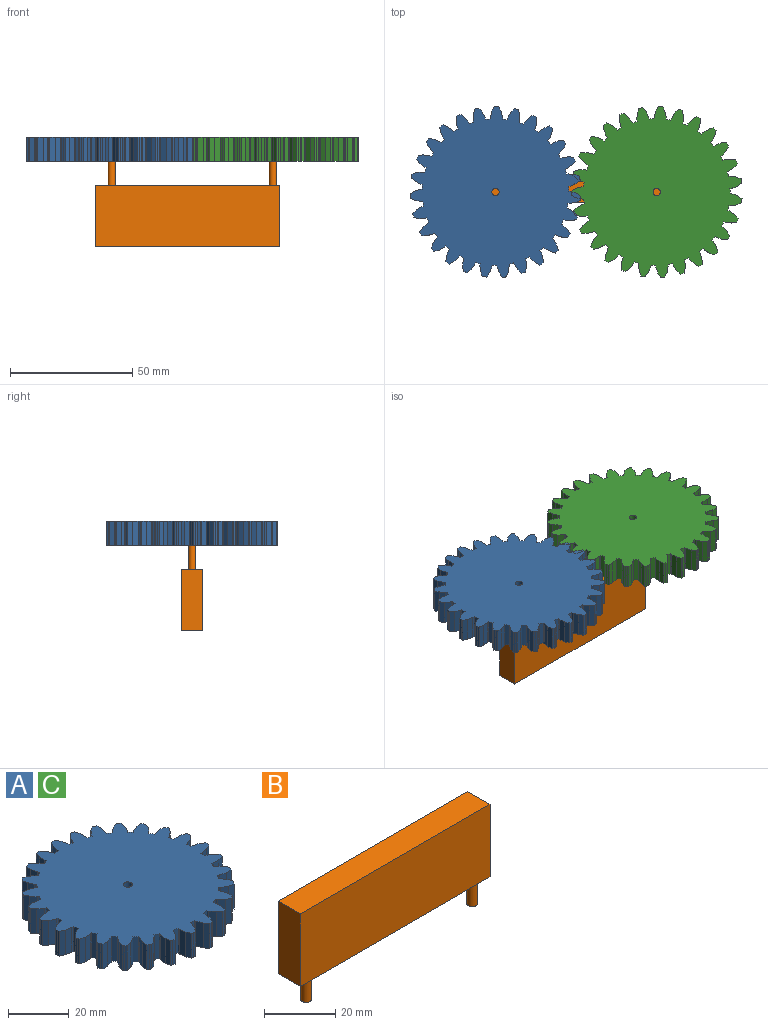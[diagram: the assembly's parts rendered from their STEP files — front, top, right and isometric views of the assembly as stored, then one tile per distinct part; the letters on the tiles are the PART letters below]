
ASSEMBLY  parts=3 mates=2
PART A: 246 faces, bbox 70x69.9x10 mm
  f0: plane 10x2.54mm, normal (0.19,-0.98,0), area 25.8mm2, adj f1,f163,f244,f245
  f1: plane 10x1.95mm, normal (0.42,-0.91,0), area 21.4mm2, adj f0,f2,f244,f245
  f2: plane 10x0.85mm, normal (1,-0.07,0), area 8.5mm2, adj f1,f3,f244,f245
  f3: plane 10x0.85mm, normal (1,-0.05,0), area 8.5mm2, adj f2,f4,f244,f245
  f4: plane 10x1.83mm, normal (0.52,0.85,0), area 21.4mm2, adj f3,f5,f244,f245
  f5: plane 10x2.46mm, normal (0.3,0.95,0), area 25.8mm2, adj f4,f164,f244,f245
  f6: plane 10x2.36mm, normal (0.41,-0.91,0), area 25.8mm2, adj f7,f166,f244,f245
  f7: plane 10x1.69mm, normal (0.62,-0.79,0), area 21.4mm2, adj f6,f8,f244,f245
  f8: plane 10x0.84mm, normal (0.99,0.16,0), area 8.5mm2, adj f7,f9,f244,f245
  f9: plane 10x0.84mm, normal (0.98,0.19,0), area 8.5mm2, adj f8,f10,f244,f245
  f10: plane 10x2.04mm, normal (0.31,0.95,0), area 21.4mm2, adj f9,f11,f244,f245
  f11: plane 10x2.58mm, normal (0.08,1,0), area 25.8mm2, adj f10,f167,f244,f245
  f12: plane 10x2.05mm, normal (0.61,-0.79,0), area 25.8mm2, adj f13,f169,f244,f245
  f13: plane 10x1.68mm, normal (0.78,-0.62,0), area 21.4mm2, adj f12,f14,f244,f245
  f14: plane 10x0.78mm, normal (0.92,0.38,0), area 8.5mm2, adj f13,f15,f244,f245
  f15: plane 10x0.78mm, normal (0.91,0.41,0), area 8.5mm2, adj f14,f16,f244,f245
  f16: plane 10x2.14mm, normal (0.08,1,0), area 21.4mm2, adj f15,f17,f244,f245
  f17: plane 10x2.55mm, normal (-0.16,0.99,0), area 25.8mm2, adj f16,f170,f244,f245
  f18: plane 10x2.01mm, normal (0.78,-0.63,0), area 25.8mm2, adj f19,f172,f244,f245
  f19: plane 10x1.94mm, normal (0.9,-0.43,0), area 21.4mm2, adj f18,f20,f244,f245
  f20: plane 10x0.69mm, normal (0.81,0.59,0), area 8.5mm2, adj f19,f21,f244,f245
  f21: plane 10x0.68mm, normal (0.79,0.61,0), area 8.5mm2, adj f20,f22,f244,f245
  f22: plane 10x2.12mm, normal (-0.15,0.99,0), area 21.4mm2, adj f21,f23,f244,f245
  f23: plane 10x2.39mm, normal (-0.38,0.92,0), area 25.8mm2, adj f22,f173,f244,f245
  f24: plane 10x2.33mm, normal (0.9,-0.43,0), area 25.8mm2, adj f25,f175,f244,f245
  f25: plane 10x2.1mm, normal (0.98,-0.21,0), area 21.4mm2, adj f24,f26,f244,f245
  f26: plane 10x0.64mm, normal (0.65,0.76,0), area 8.5mm2, adj f25,f27,f244,f245
  f27: plane 10x0.66mm, normal (0.63,0.77,0), area 8.5mm2, adj f26,f28,f244,f245
  f28: plane 10x1.99mm, normal (-0.37,0.93,0), area 21.4mm2, adj f27,f29,f244,f245
  f29: plane 10x2.1mm, normal (-0.58,0.81,0), area 25.8mm2, adj f28,f176,f244,f245
  f30: plane 10x2.53mm, normal (0.98,-0.21,0), area 25.8mm2, adj f31,f178,f244,f245
  f31: plane 10x2.14mm, normal (1,0.03,0), area 21.4mm2, adj f30,f32,f244,f245
  f32: plane 10x0.76mm, normal (0.46,0.89,0), area 8.5mm2, adj f31,f33,f244,f245
  f33: plane 10x0.76mm, normal (0.44,0.9,0), area 8.5mm2, adj f32,f34,f244,f245
  f34: plane 10x1.75mm, normal (-0.58,0.82,0), area 21.4mm2, adj f33,f35,f244,f245
  f35: plane 10x1.95mm, normal (-0.75,0.66,0), area 25.8mm2, adj f34,f179,f244,f245
  f36: plane 10x2.58mm, normal (1,0.02,0), area 25.8mm2, adj f37,f181,f244,f245
  f37: plane 10x2.07mm, normal (0.97,0.26,0), area 21.4mm2, adj f36,f38,f244,f245
  f38: plane 10x0.82mm, normal (0.24,0.97,0), area 8.5mm2, adj f37,f39,f244,f245
  f39: plane 10x0.83mm, normal (0.22,0.98,0), area 8.5mm2, adj f38,f40,f244,f245
  f40: plane 10x1.61mm, normal (-0.75,0.66,0), area 21.4mm2, adj f39,f41,f244,f245
  f41: plane 10x2.29mm, normal (-0.89,0.46,0), area 25.8mm2, adj f40,f182,f244,f245
  f42: plane 10x2.5mm, normal (0.97,0.25,0), area 25.8mm2, adj f43,f184,f244,f245
  f43: plane 10x1.89mm, normal (0.88,0.47,0), area 21.4mm2, adj f42,f44,f244,f245
  f44: plane 10x0.85mm, normal (0.01,1,0), area 8.5mm2, adj f43,f45,f244,f245
  f45: plane 10x0.85mm, normal (-0.01,1,0), area 8.5mm2, adj f44,f46,f244,f245
  f46: plane 10x1.89mm, normal (-0.88,0.47,0), area 21.4mm2, adj f45,f47,f244,f245
  f47: plane 10x2.5mm, normal (-0.97,0.25,0), area 25.8mm2, adj f46,f185,f244,f245
  f48: plane 10x2.29mm, normal (0.89,0.46,0), area 25.8mm2, adj f49,f187,f244,f245
  f49: plane 10x1.61mm, normal (0.75,0.66,0), area 21.4mm2, adj f48,f50,f244,f245
  f50: plane 10x0.83mm, normal (-0.22,0.98,0), area 8.5mm2, adj f49,f51,f244,f245
  f51: plane 10x0.82mm, normal (-0.24,0.97,0), area 8.5mm2, adj f50,f52,f244,f245
  f52: plane 10x2.07mm, normal (-0.97,0.26,0), area 21.4mm2, adj f51,f53,f244,f245
  f53: plane 10x2.58mm, normal (-1,0.02,0), area 25.8mm2, adj f52,f188,f244,f245
  f54: plane 10x1.95mm, normal (0.75,0.66,0), area 25.8mm2, adj f55,f190,f244,f245
  f55: plane 10x1.75mm, normal (0.58,0.82,0), area 21.4mm2, adj f54,f56,f244,f245
  f56: plane 10x0.76mm, normal (-0.44,0.9,0), area 8.5mm2, adj f55,f57,f244,f245
  f57: plane 10x0.76mm, normal (-0.46,0.89,0), area 8.5mm2, adj f56,f58,f244,f245
  f58: plane 10x2.14mm, normal (-1,0.03,0), area 21.4mm2, adj f57,f59,f244,f245
  f59: plane 10x2.53mm, normal (-0.98,-0.21,0), area 25.8mm2, adj f58,f191,f244,f245
  f60: plane 10x2.1mm, normal (0.58,0.81,0), area 25.8mm2, adj f61,f193,f244,f245
  f61: plane 10x1.99mm, normal (0.37,0.93,0), area 21.4mm2, adj f60,f62,f244,f245
  f62: plane 10x0.66mm, normal (-0.63,0.77,0), area 8.5mm2, adj f61,f63,f244,f245
  f63: plane 10x0.64mm, normal (-0.65,0.76,0), area 8.5mm2, adj f62,f64,f244,f245
  f64: plane 10x2.1mm, normal (-0.98,-0.21,0), area 21.4mm2, adj f63,f65,f244,f245
  f65: plane 10x2.33mm, normal (-0.9,-0.43,0), area 25.8mm2, adj f64,f194,f244,f245
  f66: plane 10x2.39mm, normal (0.38,0.92,0), area 25.8mm2, adj f67,f196,f244,f245
  f67: plane 10x2.12mm, normal (0.15,0.99,0), area 21.4mm2, adj f66,f68,f244,f245
  f68: plane 10x0.68mm, normal (-0.79,0.61,0), area 8.5mm2, adj f67,f69,f244,f245
  f69: plane 10x0.69mm, normal (-0.81,0.59,0), area 8.5mm2, adj f68,f70,f244,f245
  f70: plane 10x1.94mm, normal (-0.9,-0.43,0), area 21.4mm2, adj f69,f71,f244,f245
  f71: plane 10x2.01mm, normal (-0.78,-0.63,0), area 25.8mm2, adj f70,f197,f244,f245
  f72: plane 10x2.55mm, normal (0.16,0.99,0), area 25.8mm2, adj f73,f199,f244,f245
  f73: plane 10x2.14mm, normal (-0.08,1,0), area 21.4mm2, adj f72,f74,f244,f245
  f74: plane 10x0.78mm, normal (-0.91,0.41,0), area 8.5mm2, adj f73,f75,f244,f245
  f75: plane 10x0.78mm, normal (-0.92,0.38,0), area 8.5mm2, adj f74,f76,f244,f245
  f76: plane 10x1.68mm, normal (-0.78,-0.62,0), area 21.4mm2, adj f75,f77,f244,f245
  f77: plane 10x2.05mm, normal (-0.61,-0.79,0), area 25.8mm2, adj f76,f200,f244,f245
  f78: plane 10x2.58mm, normal (-0.08,1,0), area 25.8mm2, adj f79,f202,f244,f245
  f79: plane 10x2.04mm, normal (-0.31,0.95,0), area 21.4mm2, adj f78,f80,f244,f245
  f80: plane 10x0.84mm, normal (-0.98,0.19,0), area 8.5mm2, adj f79,f81,f244,f245
  f81: plane 10x0.84mm, normal (-0.99,0.16,0), area 8.5mm2, adj f80,f82,f244,f245
  f82: plane 10x1.69mm, normal (-0.62,-0.79,0), area 21.4mm2, adj f81,f83,f244,f245
  f83: plane 10x2.36mm, normal (-0.41,-0.91,0), area 25.8mm2, adj f82,f203,f244,f245
  f84: plane 10x2.46mm, normal (-0.3,0.95,0), area 25.8mm2, adj f85,f205,f244,f245
  f85: plane 10x1.83mm, normal (-0.52,0.85,0), area 21.4mm2, adj f84,f86,f244,f245
  f86: plane 10x0.85mm, normal (-1,-0.05,0), area 8.5mm2, adj f85,f87,f244,f245
  f87: plane 10x0.85mm, normal (-1,-0.07,0), area 8.5mm2, adj f86,f88,f244,f245
  f88: plane 10x1.95mm, normal (-0.42,-0.91,0), area 21.4mm2, adj f87,f89,f244,f245
  f89: plane 10x2.54mm, normal (-0.19,-0.98,0), area 25.8mm2, adj f88,f206,f244,f245
  f90: plane 10x2.22mm, normal (-0.51,0.86,0), area 25.8mm2, adj f91,f208,f244,f245
  f91: plane 10x1.52mm, normal (-0.7,0.71,0), area 21.4mm2, adj f90,f92,f244,f245
  f92: plane 10x0.82mm, normal (-0.96,-0.28,0), area 8.5mm2, adj f91,f93,f244,f245
  f93: plane 10x0.81mm, normal (-0.95,-0.3,0), area 8.5mm2, adj f92,f94,f244,f245
  f94: plane 10x2.1mm, normal (-0.2,-0.98,0), area 21.4mm2, adj f93,f95,f244,f245
  f95: plane 10x2.58mm, normal (0.04,-1,0), area 25.8mm2, adj f94,f209,f244,f245
  f96: plane 10x1.85mm, normal (-0.7,0.72,0), area 25.8mm2, adj f97,f211,f244,f245
  f97: plane 10x1.82mm, normal (-0.85,0.53,0), area 21.4mm2, adj f96,f98,f244,f245
  f98: plane 10x0.74mm, normal (-0.87,-0.49,0), area 8.5mm2, adj f97,f99,f244,f245
  f99: plane 10x0.73mm, normal (-0.86,-0.51,0), area 8.5mm2, adj f98,f100,f244,f245
  f100: plane 10x2.14mm, normal (0.03,-1,0), area 21.4mm2, adj f99,f101,f244,f245
  f101: plane 10x2.49mm, normal (0.27,-0.96,0), area 25.8mm2, adj f100,f212,f244,f245
  f102: plane 10x2.18mm, normal (-0.84,0.54,0), area 25.8mm2, adj f103,f214,f244,f245
  f103: plane 10x2.03mm, normal (-0.95,0.32,0), area 21.4mm2, adj f102,f104,f244,f245
  f104: plane 10x0.63mm, normal (-0.74,-0.68,0), area 8.5mm2, adj f103,f105,f244,f245
  f105: plane 10x0.61mm, normal (-0.72,-0.7,0), area 8.5mm2, adj f104,f106,f244,f245
  f106: plane 10x2.07mm, normal (0.26,-0.97,0), area 21.4mm2, adj f105,f107,f244,f245
  f107: plane 10x2.26mm, normal (0.49,-0.87,0), area 25.8mm2, adj f106,f215,f244,f245
  f108: plane 10x2.44mm, normal (-0.95,0.33,0), area 25.8mm2, adj f109,f217,f244,f245
  f109: plane 10x2.13mm, normal (-1,0.09,0), area 21.4mm2, adj f108,f110,f244,f245
  f110: plane 10x0.7mm, normal (-0.56,-0.83,0), area 8.5mm2, adj f109,f111,f244,f245
  f111: plane 10x0.72mm, normal (-0.54,-0.84,0), area 8.5mm2, adj f110,f112,f244,f245
  f112: plane 10x1.88mm, normal (0.48,-0.88,0), area 21.4mm2, adj f111,f113,f244,f245
  f113: plane 10x1.91mm, normal (0.67,-0.74,0), area 25.8mm2, adj f112,f218,f244,f245
  f114: plane 10x2.57mm, normal (-1,0.1,0), area 25.8mm2, adj f115,f220,f244,f245
  f115: plane 10x2.12mm, normal (-0.99,-0.14,0), area 21.4mm2, adj f114,f116,f244,f245
  f116: plane 10x0.8mm, normal (-0.35,-0.94,0), area 8.5mm2, adj f115,f117,f244,f245
  f117: plane 10x0.8mm, normal (-0.33,-0.94,0), area 8.5mm2, adj f116,f118,f244,f245
  f118: plane 10x1.6mm, normal (0.67,-0.74,0), area 21.4mm2, adj f117,f119,f244,f245
  f119: plane 10x2.14mm, normal (0.83,-0.56,0), area 25.8mm2, adj f118,f221,f244,f245
  f120: plane 10x2.56mm, normal (-0.99,-0.13,0), area 25.8mm2, adj f121,f223,f244,f245
  f121: plane 10x1.99mm, normal (-0.93,-0.37,0), area 21.4mm2, adj f120,f122,f244,f245
  f122: plane 10x0.84mm, normal (-0.13,-0.99,0), area 8.5mm2, adj f121,f123,f244,f245
  f123: plane 10x0.85mm, normal (-0.1,-0.99,0), area 8.5mm2, adj f122,f124,f244,f245
  f124: plane 10x1.76mm, normal (0.82,-0.57,0), area 21.4mm2, adj f123,f125,f244,f245
  f125: plane 10x2.41mm, normal (0.93,-0.36,0), area 25.8mm2, adj f124,f224,f244,f245
  f126: plane 10x2.41mm, normal (-0.93,-0.36,0), area 25.8mm2, adj f127,f226,f244,f245
  f127: plane 10x1.76mm, normal (-0.82,-0.57,0), area 21.4mm2, adj f126,f128,f244,f245
  f128: plane 10x0.85mm, normal (0.1,-0.99,0), area 8.5mm2, adj f127,f129,f244,f245
  f129: plane 10x0.84mm, normal (0.13,-0.99,0), area 8.5mm2, adj f128,f130,f244,f245
  f130: plane 10x1.99mm, normal (0.93,-0.37,0), area 21.4mm2, adj f129,f131,f244,f245
  f131: plane 10x2.56mm, normal (0.99,-0.13,0), area 25.8mm2, adj f130,f227,f244,f245
  f132: plane 10x2.14mm, normal (-0.83,-0.56,0), area 25.8mm2, adj f133,f229,f244,f245
  f133: plane 10x1.6mm, normal (-0.67,-0.74,0), area 21.4mm2, adj f132,f134,f244,f245
  f134: plane 10x0.8mm, normal (0.33,-0.94,0), area 8.5mm2, adj f133,f135,f244,f245
  f135: plane 10x0.8mm, normal (0.35,-0.94,0), area 8.5mm2, adj f134,f136,f244,f245
  f136: plane 10x2.12mm, normal (0.99,-0.14,0), area 21.4mm2, adj f135,f137,f244,f245
  f137: plane 10x2.57mm, normal (1,0.1,0), area 25.8mm2, adj f136,f230,f244,f245
  f138: plane 10x1.91mm, normal (-0.67,-0.74,0), area 25.8mm2, adj f139,f232,f244,f245
  f139: plane 10x1.88mm, normal (-0.48,-0.88,0), area 21.4mm2, adj f138,f140,f244,f245
  f140: plane 10x0.72mm, normal (0.54,-0.84,0), area 8.5mm2, adj f139,f141,f244,f245
  f141: plane 10x0.7mm, normal (0.56,-0.83,0), area 8.5mm2, adj f140,f142,f244,f245
  f142: plane 10x2.13mm, normal (1,0.09,0), area 21.4mm2, adj f141,f143,f244,f245
  f143: plane 10x2.44mm, normal (0.95,0.33,0), area 25.8mm2, adj f142,f233,f244,f245
  f144: plane 10x2.26mm, normal (-0.49,-0.87,0), area 25.8mm2, adj f145,f235,f244,f245
  f145: plane 10x2.07mm, normal (-0.26,-0.97,0), area 21.4mm2, adj f144,f146,f244,f245
  f146: plane 10x0.61mm, normal (0.72,-0.7,0), area 8.5mm2, adj f145,f147,f244,f245
  f147: plane 10x0.63mm, normal (0.74,-0.68,0), area 8.5mm2, adj f146,f148,f244,f245
  f148: plane 10x2.03mm, normal (0.95,0.32,0), area 21.4mm2, adj f147,f149,f244,f245
  f149: plane 10x2.18mm, normal (0.84,0.54,0), area 25.8mm2, adj f148,f236,f244,f245
  f150: plane 10x2.49mm, normal (-0.27,-0.96,0), area 25.8mm2, adj f151,f238,f244,f245
  f151: plane 10x2.14mm, normal (-0.03,-1,0), area 21.4mm2, adj f150,f152,f244,f245
  f152: plane 10x0.73mm, normal (0.86,-0.51,0), area 8.5mm2, adj f151,f153,f244,f245
  f153: plane 10x0.74mm, normal (0.87,-0.49,0), area 8.5mm2, adj f152,f154,f244,f245
  f154: plane 10x1.82mm, normal (0.85,0.53,0), area 21.4mm2, adj f153,f155,f244,f245
  f155: plane 10x1.85mm, normal (0.7,0.72,0), area 25.8mm2, adj f154,f239,f244,f245
  f156: plane 10x2.58mm, normal (-0.04,-1,0), area 25.8mm2, adj f157,f241,f244,f245
  f157: plane 10x2.1mm, normal (0.2,-0.98,0), area 21.4mm2, adj f156,f158,f244,f245
  f158: plane 10x0.81mm, normal (0.95,-0.3,0), area 8.5mm2, adj f157,f159,f244,f245
  f159: plane 10x0.82mm, normal (0.96,-0.28,0), area 8.5mm2, adj f158,f160,f244,f245
  f160: plane 10x1.52mm, normal (0.7,0.71,0), area 21.4mm2, adj f159,f161,f244,f245
  f161: plane 10x2.22mm, normal (0.51,0.86,0), area 25.8mm2, adj f160,f243,f244,f245
  f162: cylinder r=30mm len=10mm, axis (0,0,-1), area 19.8mm2, adj f163,f243,f244,f245
  f163: plane 10x0.7mm, normal (-0.06,-1,0), area 7mm2, adj f0,f162,f244,f245
  f164: plane 10x0.7mm, normal (0.06,1,0), area 7mm2, adj f5,f165,f244,f245
  f165: cylinder r=30mm len=10mm, axis (0,0,-1), area 19.8mm2, adj f164,f166,f244,f245
  f166: plane 10x0.69mm, normal (0.17,-0.98,0), area 7mm2, adj f6,f165,f244,f245
  f167: plane 10x0.69mm, normal (-0.17,0.98,0), area 7mm2, adj f11,f168,f244,f245
  f168: cylinder r=30mm len=10mm, axis (0,0,-1), area 19.8mm2, adj f167,f169,f244,f245
  f169: plane 10x0.64mm, normal (0.4,-0.92,0), area 7mm2, adj f12,f168,f244,f245
  f170: plane 10x0.64mm, normal (-0.4,0.92,0), area 7mm2, adj f17,f171,f244,f245
  f171: cylinder r=30mm len=10mm, axis (0,0,-1), area 19.8mm2, adj f170,f172,f244,f245
  f172: plane 10x0.56mm, normal (0.6,-0.8,0), area 7mm2, adj f18,f171,f244,f245
  f173: plane 10x0.56mm, normal (-0.6,0.8,0), area 7mm2, adj f23,f174,f244,f245
  f174: cylinder r=30mm len=10mm, axis (0,0,-1), area 19.8mm2, adj f173,f175,f244,f245
  f175: plane 10x0.54mm, normal (0.77,-0.64,0), area 7mm2, adj f24,f174,f244,f245
  f176: plane 10x0.54mm, normal (-0.77,0.64,0), area 7mm2, adj f29,f177,f244,f245
  f177: cylinder r=30mm len=10mm, axis (0,0,-1), area 19.8mm2, adj f176,f178,f244,f245
  f178: plane 10x0.63mm, normal (0.89,-0.45,0), area 7mm2, adj f30,f177,f244,f245
  f179: plane 10x0.63mm, normal (-0.89,0.45,0), area 7mm2, adj f35,f180,f244,f245
  f180: cylinder r=30mm len=10mm, axis (0,0,-1), area 19.8mm2, adj f179,f181,f244,f245
  f181: plane 10x0.68mm, normal (0.97,-0.23,0), area 7mm2, adj f36,f180,f244,f245
  f182: plane 10x0.68mm, normal (-0.97,0.23,0), area 7mm2, adj f41,f183,f244,f245
  f183: cylinder r=30mm len=10mm, axis (0,0,-1), area 19.8mm2, adj f182,f184,f244,f245
  f184: plane 10x0.7mm, normal (1,0,0), area 7mm2, adj f42,f183,f244,f245
  f185: plane 10x0.7mm, normal (-1,0,0), area 7mm2, adj f47,f186,f244,f245
  f186: cylinder r=30mm len=10mm, axis (0,0,-1), area 19.8mm2, adj f185,f187,f244,f245
  f187: plane 10x0.68mm, normal (0.97,0.23,0), area 7mm2, adj f48,f186,f244,f245
  f188: plane 10x0.68mm, normal (-0.97,-0.23,0), area 7mm2, adj f53,f189,f244,f245
  f189: cylinder r=30mm len=10mm, axis (0,0,-1), area 19.8mm2, adj f188,f190,f244,f245
  f190: plane 10x0.63mm, normal (0.89,0.45,0), area 7mm2, adj f54,f189,f244,f245
  f191: plane 10x0.63mm, normal (-0.89,-0.45,0), area 7mm2, adj f59,f192,f244,f245
  f192: cylinder r=30mm len=10mm, axis (0,0,-1), area 19.8mm2, adj f191,f193,f244,f245
  f193: plane 10x0.54mm, normal (0.77,0.64,0), area 7mm2, adj f60,f192,f244,f245
  f194: plane 10x0.54mm, normal (-0.77,-0.64,0), area 7mm2, adj f65,f195,f244,f245
  f195: cylinder r=30mm len=10mm, axis (0,0,-1), area 19.8mm2, adj f194,f196,f244,f245
  f196: plane 10x0.56mm, normal (0.6,0.8,0), area 7mm2, adj f66,f195,f244,f245
  f197: plane 10x0.56mm, normal (-0.6,-0.8,0), area 7mm2, adj f71,f198,f244,f245
  f198: cylinder r=30mm len=10mm, axis (0,0,-1), area 19.8mm2, adj f197,f199,f244,f245
  f199: plane 10x0.64mm, normal (0.4,0.92,0), area 7mm2, adj f72,f198,f244,f245
  f200: plane 10x0.64mm, normal (-0.4,-0.92,0), area 7mm2, adj f77,f201,f244,f245
  f201: cylinder r=30mm len=10mm, axis (0,0,-1), area 19.8mm2, adj f200,f202,f244,f245
  f202: plane 10x0.69mm, normal (0.17,0.98,0), area 7mm2, adj f78,f201,f244,f245
  f203: plane 10x0.69mm, normal (-0.17,-0.98,0), area 7mm2, adj f83,f204,f244,f245
  f204: cylinder r=30mm len=10mm, axis (0,0,-1), area 19.8mm2, adj f203,f205,f244,f245
  f205: plane 10x0.7mm, normal (-0.06,1,0), area 7mm2, adj f84,f204,f244,f245
  f206: plane 10x0.7mm, normal (0.06,-1,0), area 7mm2, adj f89,f207,f244,f245
  f207: cylinder r=30mm len=10mm, axis (0,0,-1), area 19.8mm2, adj f206,f208,f244,f245
  f208: plane 10x0.67mm, normal (-0.29,0.96,0), area 7mm2, adj f90,f207,f244,f245
  f209: plane 10x0.67mm, normal (0.29,-0.96,0), area 7mm2, adj f95,f210,f244,f245
  f210: cylinder r=30mm len=10mm, axis (0,0,-1), area 19.8mm2, adj f209,f211,f244,f245
  f211: plane 10x0.61mm, normal (-0.5,0.87,0), area 7mm2, adj f96,f210,f244,f245
  f212: plane 10x0.61mm, normal (0.5,-0.87,0), area 7mm2, adj f101,f213,f244,f245
  f213: cylinder r=30mm len=10mm, axis (0,0,-1), area 19.8mm2, adj f212,f214,f244,f245
  f214: plane 10x0.51mm, normal (-0.69,0.73,0), area 7mm2, adj f102,f213,f244,f245
  f215: plane 10x0.51mm, normal (0.69,-0.73,0), area 7mm2, adj f107,f216,f244,f245
  f216: cylinder r=30mm len=10mm, axis (0,0,-1), area 19.8mm2, adj f215,f217,f244,f245
  f217: plane 10x0.59mm, normal (-0.84,0.55,0), area 7mm2, adj f108,f216,f244,f245
  f218: plane 10x0.59mm, normal (0.84,-0.55,0), area 7mm2, adj f113,f219,f244,f245
  f219: cylinder r=30mm len=10mm, axis (0,0,-1), area 19.8mm2, adj f218,f220,f244,f245
  f220: plane 10x0.66mm, normal (-0.94,0.34,0), area 7mm2, adj f114,f219,f244,f245
  f221: plane 10x0.66mm, normal (0.94,-0.34,0), area 7mm2, adj f119,f222,f244,f245
  f222: cylinder r=30mm len=10mm, axis (0,0,-1), area 19.8mm2, adj f221,f223,f244,f245
  f223: plane 10x0.7mm, normal (-0.99,0.12,0), area 7mm2, adj f120,f222,f244,f245
  f224: plane 10x0.7mm, normal (0.99,-0.12,0), area 7mm2, adj f125,f225,f244,f245
  f225: cylinder r=30mm len=10mm, axis (0,0,-1), area 19.8mm2, adj f224,f226,f244,f245
  f226: plane 10x0.7mm, normal (-0.99,-0.12,0), area 7mm2, adj f126,f225,f244,f245
  f227: plane 10x0.7mm, normal (0.99,0.12,0), area 7mm2, adj f131,f228,f244,f245
  f228: cylinder r=30mm len=10mm, axis (0,0,-1), area 19.8mm2, adj f227,f229,f244,f245
  f229: plane 10x0.66mm, normal (-0.94,-0.34,0), area 7mm2, adj f132,f228,f244,f245
  f230: plane 10x0.66mm, normal (0.94,0.34,0), area 7mm2, adj f137,f231,f244,f245
  f231: cylinder r=30mm len=10mm, axis (0,0,-1), area 19.8mm2, adj f230,f232,f244,f245
  f232: plane 10x0.59mm, normal (-0.84,-0.55,0), area 7mm2, adj f138,f231,f244,f245
  f233: plane 10x0.59mm, normal (0.84,0.55,0), area 7mm2, adj f143,f234,f244,f245
  f234: cylinder r=30mm len=10mm, axis (0,0,-1), area 19.8mm2, adj f233,f235,f244,f245
  f235: plane 10x0.51mm, normal (-0.69,-0.73,0), area 7mm2, adj f144,f234,f244,f245
  f236: plane 10x0.51mm, normal (0.69,0.73,0), area 7mm2, adj f149,f237,f244,f245
  f237: cylinder r=30mm len=10mm, axis (0,0,-1), area 19.8mm2, adj f236,f238,f244,f245
  f238: plane 10x0.61mm, normal (-0.5,-0.87,0), area 7mm2, adj f150,f237,f244,f245
  f239: plane 10x0.61mm, normal (0.5,0.87,0), area 7mm2, adj f155,f240,f244,f245
  f240: cylinder r=30mm len=10mm, axis (0,0,-1), area 19.8mm2, adj f239,f241,f244,f245
  f241: plane 10x0.67mm, normal (-0.29,-0.96,0), area 7mm2, adj f156,f240,f244,f245
  f242: cylinder r=1.5mm len=10mm, axis (0,0,-1), area 94.2mm2, adj f244,f245
  f243: plane 10x0.67mm, normal (0.29,0.96,0), area 7mm2, adj f161,f162,f244,f245
  f244: plane 69.96x69.85mm, normal (0,0,-1), area 3338.9mm2, adj f0,f1,f2,f3,f4,f5,f6,f7
  f245: plane 69.96x69.85mm, normal (0,0,1), area 3338.9mm2, adj f0,f1,f2,f3,f4,f5,f6,f7
PART B: 10 faces, bbox 75.5x8.8x35 mm
  f0: plane 25x8.8mm, normal (-1,0,0), area 219.9mm2, adj f1,f3,f4,f5
  f1: plane 75.48x25mm, normal (0,-1,0), area 1887mm2, adj f0,f2,f4,f5
  f2: plane 25x8.8mm, normal (1,0,0), area 219.9mm2, adj f1,f3,f4,f5
  f3: plane 75.48x25mm, normal (0,1,0), area 1887mm2, adj f0,f2,f4,f5
  f4: plane 75.48x8.8mm, normal (0,0,1), area 664mm2, adj f0,f1,f2,f3
  f5: plane 75.48x8.8mm, normal (0,0,-1), area 649.8mm2, adj f0,f1,f2,f3,f6,f8
  f6: cylinder r=1.5mm len=10mm, axis (0,0,1), area 94.2mm2, adj f5,f7
  f7: plane 3x3mm, normal (0,0,-1), area 7.1mm2, adj f6
  f8: cylinder r=1.5mm len=10mm, axis (0,0,1), area 94.2mm2, adj f5,f9
  f9: plane 3x3mm, normal (0,0,-1), area 7.1mm2, adj f8
PART C: same geometry as A
PLACE A rot(axis=(0,0,1),172.6deg) t=(-33.73,-5.06,40.76)mm
PLACE B rot(axis=(-1,0,0),180deg) t=(-2.73,-5.06,30.76)mm fixed
PLACE C rot(axis=(0,0,-1),82.6deg) t=(32.27,-5.06,40.76)mm
MATE revolute C.f162 <-> B.f8  axis (0,0,-1) through (32.27,-5.06,40.76)mm
MATE revolute A.f162 <-> B.f6  axis (0,0,-1) through (-33.73,-5.06,40.76)mm
